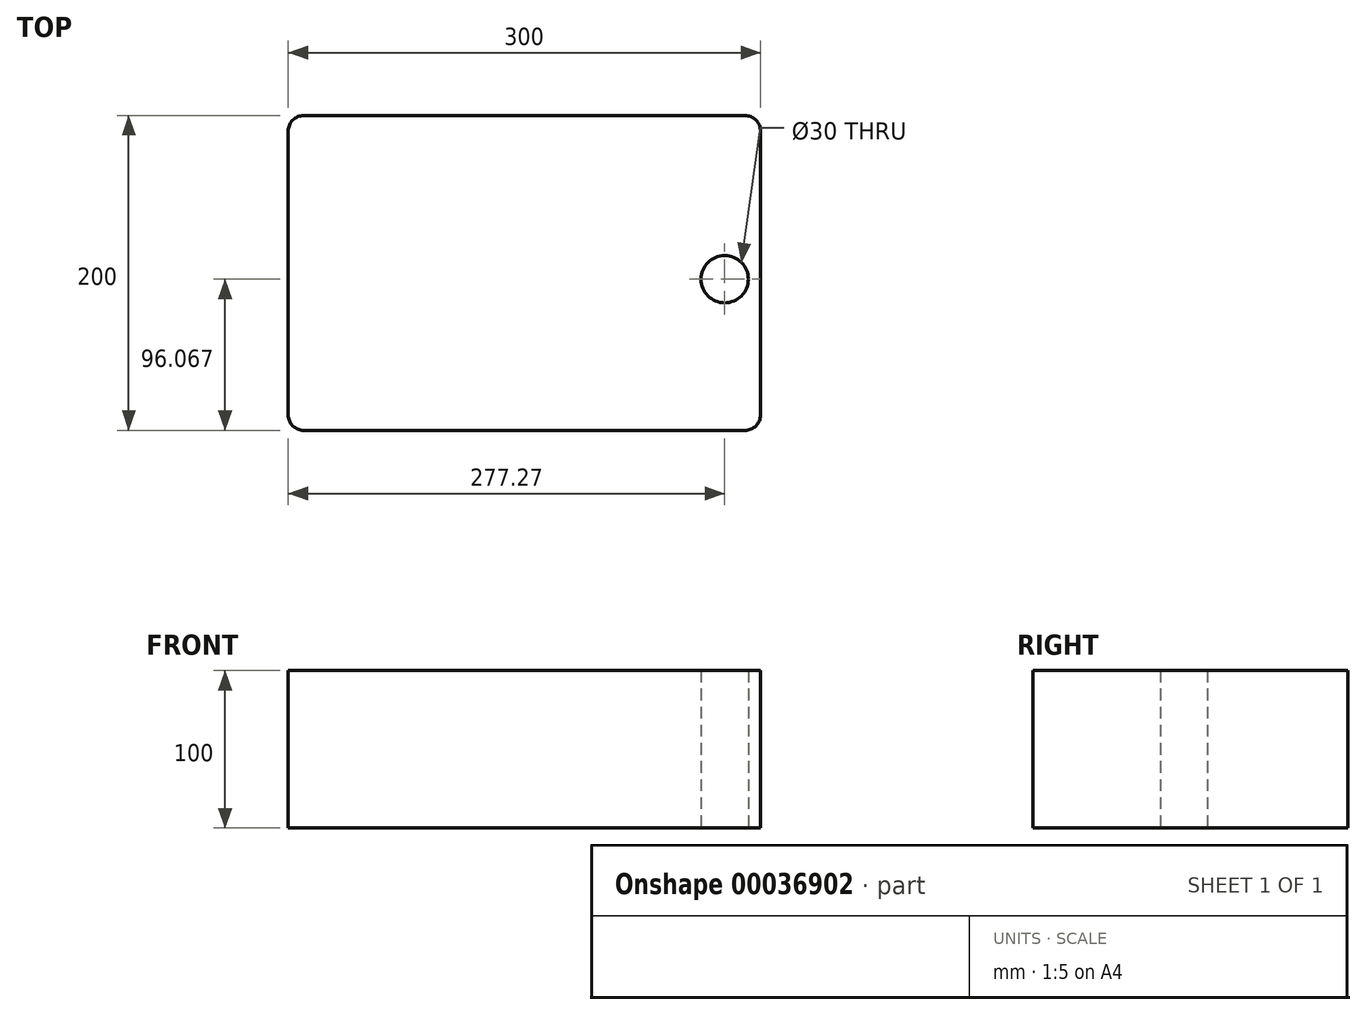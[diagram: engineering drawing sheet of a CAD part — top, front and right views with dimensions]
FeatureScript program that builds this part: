
annotation { "Feature Type Name" : "Feature", "Feature Type Description" : "" }
export const myFeature = defineFeature(function(context is Context, id is Id, definition is map)
    precondition{}
    {
        {
            var Q0;
            Q0=qCreatedBy(makeId("Top.planeOp"),FACE);
            var sketch = newSketch(context, id + "F0", { "sketchPlane" : qUnion([Q0])});
            skLineSegment(sketch, "E0.bottom", {"start": v(-147.33, 119.75) * mm, "end": v(152.67, 119.75) * mm});
            skLineSegment(sketch, "E0.top", {"start": v(-147.33, -80.25) * mm, "end": v(152.67, -80.25) * mm});
            skLineSegment(sketch, "E0.left", {"start": v(-147.33, 119.75) * mm, "end": v(-147.33, -80.25) * mm});
            skLineSegment(sketch, "E0.right", {"start": v(152.67, 119.75) * mm, "end": v(152.67, -80.25) * mm});
            skCircle(sketch, "E1", {"center": v(129.94, 15.82) * mm, "radius": 15 * mm});
            skSolve(sketch);
        }
        {
            var Q0;
            Q0 = qSketchRegion(id + "F0", true);
            extrude(context, id + "F1", {"entities" : qUnion([Q0]), "depth" : 100 * mm});
        }
        {
            var Q0;
            Q0=makeQuery(id+"F1.opExtrude","SWEPT_EDGE",EDGE,{"disambiguationData":[OSD([sQuery(id+"F0.wireOp",EDGE,"E0.bottom"),sQuery(id+"F0.wireOp",EDGE,"E0.left")])]});
            var Q1;
            Q1=makeQuery(id+"F1.opExtrude","SWEPT_EDGE",EDGE,{"disambiguationData":[OSD([sQuery(id+"F0.wireOp",EDGE,"E0.bottom"),sQuery(id+"F0.wireOp",EDGE,"E0.right")])]});
            var Q2;
            Q2=makeQuery(id+"F1.opExtrude","SWEPT_EDGE",EDGE,{"disambiguationData":[OSD([sQuery(id+"F0.wireOp",EDGE,"E0.top"),sQuery(id+"F0.wireOp",EDGE,"E0.left")])]});
            var Q3;
            Q3=makeQuery(id+"F1.opExtrude","SWEPT_EDGE",EDGE,{"disambiguationData":[OSD([sQuery(id+"F0.wireOp",EDGE,"E0.top"),sQuery(id+"F0.wireOp",EDGE,"E0.right")])]});
            fillet(context, id + "F2", {"entities" : qUnion([Q0, Q1, Q2, Q3]), "radius" : 10 * mm, "tangentPropagation" : true, "allowEdgeOverflow" : false});
        }
    });
